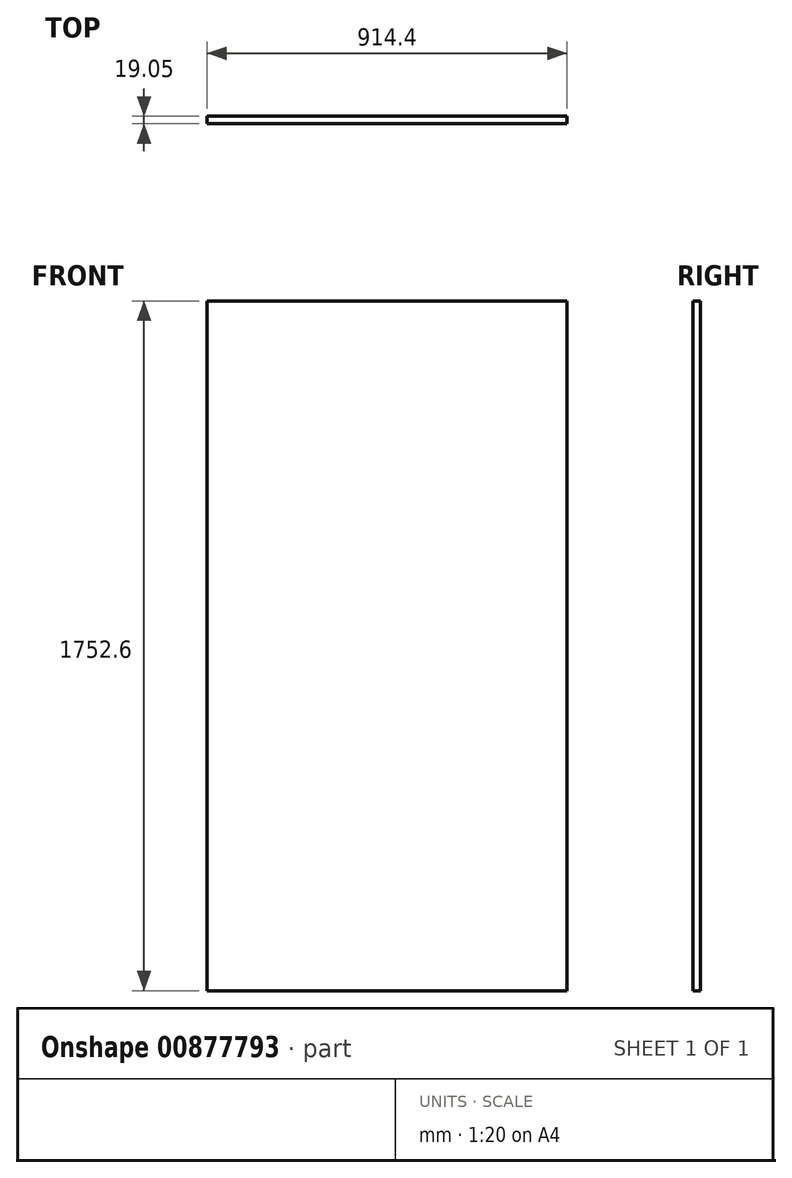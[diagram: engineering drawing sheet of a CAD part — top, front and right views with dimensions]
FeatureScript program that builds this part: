
annotation { "Feature Type Name" : "Feature", "Feature Type Description" : "" }
export const myFeature = defineFeature(function(context is Context, id is Id, definition is map)
    precondition{}
    {
        {
            var Q0;
            Q0=qCreatedBy(makeId("Front.planeOp"),FACE);
            var sketch = newSketch(context, id + "F0", { "sketchPlane" : qUnion([Q0])});
            skLineSegment(sketch, "E0.bottom", {"start": v(-581.58, 1063.17) * mm, "end": v(332.82, 1063.17) * mm});
            skLineSegment(sketch, "E0.top", {"start": v(-581.58, -689.43) * mm, "end": v(332.82, -689.43) * mm});
            skLineSegment(sketch, "E0.left", {"start": v(-581.58, 1063.17) * mm, "end": v(-581.58, -689.43) * mm});
            skLineSegment(sketch, "E0.right", {"start": v(332.82, 1063.17) * mm, "end": v(332.82, -689.43) * mm});
            skSolve(sketch);
        }
        {
            var Q0;
            Q0=makeQuery(id+"F0.imprint","IMPRINT",FACE,{"disambiguationData":[TD([[makeQuery(id+"F0.imprint","IMPRINT",EDGE,{"derivedFrom":sQuery(id+"F0.wireOp",EDGE,"E0.bottom")}),-1.0]])]});
            extrude(context, id + "F1", {"entities" : qUnion([Q0]), "depth" : 19.05 * mm, "offsetDistance" : 25.4 * mm});
        }
    });
